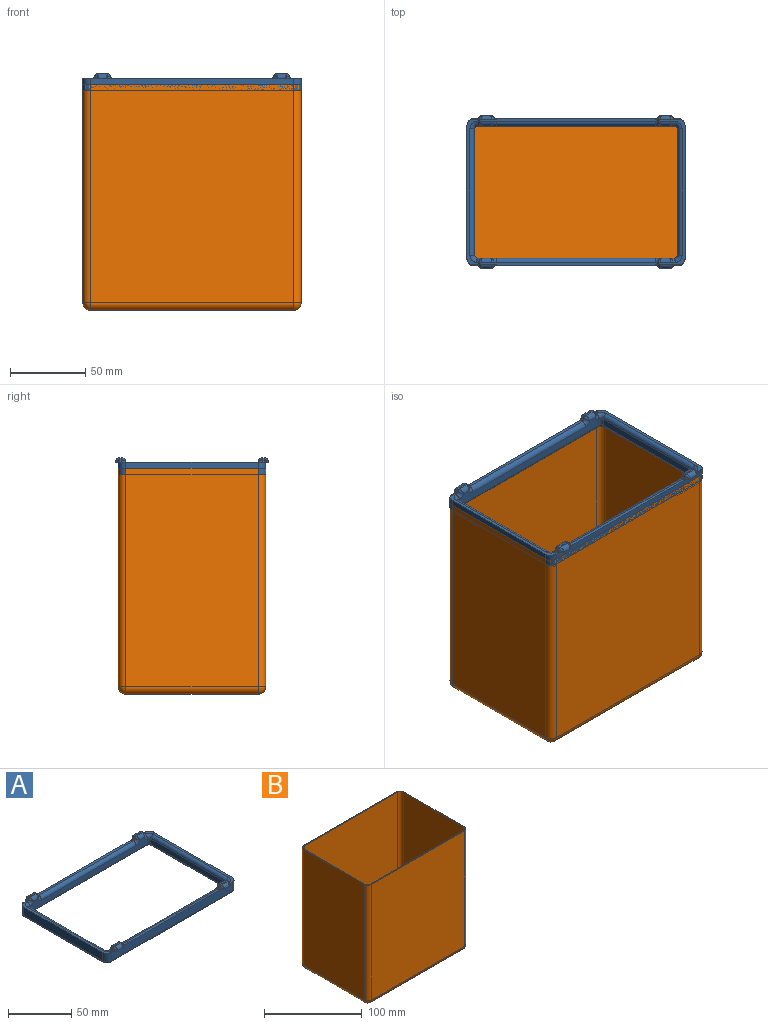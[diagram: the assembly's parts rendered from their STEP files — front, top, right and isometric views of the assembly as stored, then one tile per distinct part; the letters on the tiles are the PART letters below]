
ASSEMBLY  parts=2 mates=1
PART A: 129 faces, bbox 146.3x101.7x13.1 mm
  f0: plane 95.82x6.5mm, normal (0,0,1), area 207mm2, adj f4,f13,f16,f68,f70,f86,f88,f90
  f1: plane 105.79x2.02mm, normal (0,0,1), area 210.9mm2, adj f11,f60,f66,f73,f111,f123
  f2: plane 105.79x2.02mm, normal (0,0,1), area 210.9mm2, adj f5,f64,f72,f104,f105,f117
  f3: plane 95.82x6.5mm, normal (0,0,1), area 207mm2, adj f6,f14,f15,f58,f62,f87,f89,f91
  f4: plane 87.62x8mm, normal (1,0,0), area 701mm2, adj f0,f13,f16,f23
  f5: plane 134.77x8.83mm, normal (0,1,0), area 1078.4mm2, adj f2,f13,f14,f22,f37,f38,f39,f42
  f6: plane 87.62x8mm, normal (-1,0,0), area 701mm2, adj f3,f14,f15,f18
  f7: plane 130.77x8mm, normal (0,-1,0), area 694.7mm2, adj f30,f34,f36,f94,f95,f98,f99,f102
  f8: plane 83.62x5mm, normal (-1,0,0), area 418.1mm2, adj f27,f33,f36,f88
  f9: plane 130.77x8mm, normal (0,1,0), area 694.7mm2, adj f25,f27,f28,f73,f74,f75,f78,f79
  f10: plane 83.62x5mm, normal (1,0,0), area 418.1mm2, adj f25,f29,f30,f89
  f11: plane 134.77x8.83mm, normal (0,-1,0), area 1078.4mm2, adj f1,f15,f16,f19,f47,f48,f51,f53
  f12: plane 140.77x93.62mm, normal (0,0,-1), area 470.8mm2, adj f17,f18,f19,f20,f21,f22,f23,f24
  f13: cylinder r=5mm len=8mm, axis (0,0,-1), area 62.6mm2, adj f0,f4,f5,f24,f110
  f14: cylinder r=5mm len=8mm, axis (0,0,1), area 62.6mm2, adj f3,f5,f6,f20,f122
  f15: cylinder r=5mm len=8mm, axis (0,0,-1), area 62.6mm2, adj f3,f6,f11,f17,f128
  f16: cylinder r=5mm len=8mm, axis (0,0,1), area 62.6mm2, adj f0,f4,f11,f21,f116
  f17: torus R=3mm, axis (0,0,1), area 21.1mm2, adj f12,f15,f18,f19
  f18: cylinder r=2mm len=87.62mm, axis (0,-1,0), area 275.3mm2, adj f6,f12,f17,f20
  f19: cylinder r=2mm len=134.77mm, axis (1,0,0), area 423.4mm2, adj f11,f12,f17,f21
  f20: torus R=3mm, axis (0,0,1), area 21.1mm2, adj f12,f14,f18,f22
  f21: torus R=3mm, axis (0,0,1), area 21.1mm2, adj f12,f16,f19,f23
  f22: cylinder r=2mm len=134.77mm, axis (-1,0,0), area 423.4mm2, adj f5,f12,f20,f24
  f23: cylinder r=2mm len=87.62mm, axis (0,1,0), area 275.3mm2, adj f4,f12,f21,f24
  f24: torus R=3mm, axis (0,0,1), area 21.1mm2, adj f12,f13,f22,f23
  f25: cylinder r=2mm len=5.03mm, axis (0,0,1), area 15.7mm2, adj f9,f10,f26,f85,f87
  f26: torus R=4mm, axis (0,0,1), area 13.5mm2, adj f12,f25,f28,f29
  f27: cylinder r=2mm len=5.03mm, axis (0,0,-1), area 15.7mm2, adj f8,f9,f31,f84,f86
  f28: cylinder r=2mm len=130.77mm, axis (-1,0,0), area 410.8mm2, adj f9,f12,f26,f31
  f29: cylinder r=2mm len=83.62mm, axis (0,1,0), area 262.7mm2, adj f10,f12,f26,f32
  f30: cylinder r=2mm len=5.03mm, axis (0,0,-1), area 15.7mm2, adj f7,f10,f32,f91,f93
  f31: torus R=4mm, axis (0,0,1), area 13.5mm2, adj f12,f27,f28,f33
  f32: torus R=4mm, axis (0,0,1), area 13.5mm2, adj f12,f29,f30,f34
  f33: cylinder r=2mm len=83.62mm, axis (0,-1,0), area 262.7mm2, adj f8,f12,f31,f35
  f34: cylinder r=2mm len=130.77mm, axis (1,0,0), area 410.8mm2, adj f7,f12,f32,f35
  f35: torus R=4mm, axis (0,0,1), area 13.5mm2, adj f12,f33,f34,f36
  f36: cylinder r=2mm len=5.03mm, axis (0,0,1), area 15.7mm2, adj f7,f8,f35,f90,f92
  f37: plane 10x2mm, normal (0,0,-1), area 18.1mm2, adj f5,f38,f39,f40,f117,f121
  f38: plane 0.95x0.89mm, normal (-1,0,0), area 0.4mm2, adj f5,f37,f121
  f39: plane 0.96x0.89mm, normal (1,0,0), area 0.4mm2, adj f5,f37,f117
  f40: plane 4.73x0.1mm, normal (0,1,0), area 0.5mm2, adj f37,f117,f119,f121
  f41: plane 7x1.1mm, normal (0,0,1), area 7.7mm2, adj f61,f63,f99,f119
  f42: plane 10x2mm, normal (0,0,-1), area 18.1mm2, adj f5,f43,f44,f45,f105,f109
  f43: plane 0.96x0.89mm, normal (-1,0,0), area 0.4mm2, adj f5,f42,f105
  f44: plane 0.95x0.89mm, normal (1,0,0), area 0.4mm2, adj f5,f42,f109
  f45: plane 4.73x0.1mm, normal (0,1,0), area 0.5mm2, adj f42,f105,f107,f109
  f46: plane 7x1.1mm, normal (0,0,1), area 7.7mm2, adj f69,f71,f98,f107
  f47: plane 0.96x0.89mm, normal (1,0,0), area 0.4mm2, adj f11,f51,f123
  f48: plane 0.95x0.89mm, normal (-1,0,0), area 0.4mm2, adj f11,f51,f127
  f49: plane 4.73x0.1mm, normal (0,-1,0), area 0.5mm2, adj f51,f123,f125,f127
  f50: plane 7x1.1mm, normal (0,0,1), area 7.7mm2, adj f57,f59,f79,f125
  f51: plane 10x2mm, normal (0,0,-1), area 18.1mm2, adj f11,f47,f48,f49,f123,f127
  f52: plane 4.73x0.1mm, normal (0,-1,0), area 0.5mm2, adj f56,f111,f113,f115
  f53: plane 0.95x0.89mm, normal (1,0,0), area 0.4mm2, adj f11,f56,f115
  f54: plane 0.96x0.89mm, normal (-1,0,0), area 0.4mm2, adj f11,f56,f111
  f55: plane 7x1.1mm, normal (0,0,1), area 7.7mm2, adj f65,f67,f78,f113
  f56: plane 10x2mm, normal (0,0,-1), area 18.1mm2, adj f11,f52,f53,f54,f111,f115
  f57: cylinder r=1.5mm len=1.5mm, axis (0,1,0), area 2.6mm2, adj f50,f58,f81,f126
  f58: cylinder r=1.5mm len=1.5mm, axis (0,-1,0), area 2.6mm2, adj f3,f57,f83,f85,f127
  f59: cylinder r=1.5mm len=1.5mm, axis (0,-1,0), area 2.6mm2, adj f50,f60,f77,f124
  f60: cylinder r=1.5mm len=1.5mm, axis (0,1,0), area 2.6mm2, adj f1,f59,f75,f123
  f61: cylinder r=1.5mm len=1.5mm, axis (0,1,0), area 2.6mm2, adj f41,f62,f97,f120
  f62: cylinder r=1.5mm len=1.5mm, axis (0,-1,0), area 2.6mm2, adj f3,f61,f93,f95,f121
  f63: cylinder r=1.5mm len=1.5mm, axis (0,-1,0), area 2.6mm2, adj f41,f64,f101,f118
  f64: cylinder r=1.5mm len=1.5mm, axis (0,1,0), area 2.6mm2, adj f2,f63,f103,f117
  f65: cylinder r=1.5mm len=1.5mm, axis (0,1,0), area 2.6mm2, adj f55,f66,f76,f112
  f66: cylinder r=1.5mm len=1.5mm, axis (0,-1,0), area 2.6mm2, adj f1,f65,f74,f111
  f67: cylinder r=1.5mm len=1.5mm, axis (0,-1,0), area 2.6mm2, adj f55,f68,f80,f114
  f68: cylinder r=1.5mm len=1.5mm, axis (0,1,0), area 2.6mm2, adj f0,f67,f82,f84,f115
  f69: cylinder r=1.5mm len=1.5mm, axis (0,-1,0), area 2.6mm2, adj f46,f70,f96,f108
  f70: cylinder r=1.5mm len=1.5mm, axis (0,1,0), area 2.6mm2, adj f0,f69,f92,f94,f109
  f71: cylinder r=1.5mm len=1.5mm, axis (0,1,0), area 2.6mm2, adj f46,f72,f100,f106
  f72: cylinder r=1.5mm len=1.5mm, axis (0,-1,0), area 2.6mm2, adj f2,f71,f102,f105
  f73: cylinder r=3mm len=105.77mm, axis (1,0,0), area 498.4mm2, adj f1,f9,f74,f75
  f74: torus R=4.5mm, axis (0,-1,0), area 16.7mm2, adj f9,f66,f73,f76
  f75: torus R=4.5mm, axis (0,-1,0), area 16.7mm2, adj f9,f60,f73,f77
  f76: bspline ~3.79x3mm, area 6.2mm2, adj f65,f74,f78
  f77: bspline ~3.79x3mm, area 6.1mm2, adj f59,f75,f79
  f78: cylinder r=3mm len=7mm, axis (1,0,0), area 27.1mm2, adj f9,f55,f76,f80
  f79: cylinder r=3mm len=7mm, axis (1,0,0), area 27.1mm2, adj f9,f50,f77,f81
  f80: bspline ~3.79x3mm, area 6.1mm2, adj f67,f78,f82
  f81: bspline ~3.79x3mm, area 6.2mm2, adj f57,f79,f83
  f82: torus R=4.5mm, axis (0,-1,0), area 15.3mm2, adj f9,f68,f80,f84
  f83: torus R=4.5mm, axis (0,-1,0), area 15.3mm2, adj f9,f58,f81,f85
  f84: bspline ~3.07x3.06mm, area 0.5mm2, adj f27,f68,f82,f86
  f85: bspline ~3.07x3.06mm, area 0.5mm2, adj f25,f58,f83,f87
  f86: torus R=5mm, axis (0,0,1), area 21.4mm2, adj f0,f27,f84,f88
  f87: torus R=5mm, axis (0,0,1), area 21.4mm2, adj f3,f25,f85,f89
  f88: cylinder r=3mm len=83.62mm, axis (0,1,0), area 394mm2, adj f0,f8,f86,f90
  f89: cylinder r=3mm len=83.62mm, axis (0,-1,0), area 394mm2, adj f3,f10,f87,f91
  f90: torus R=5mm, axis (0,0,1), area 21.4mm2, adj f0,f36,f88,f92
  f91: torus R=5mm, axis (0,0,1), area 21.4mm2, adj f3,f30,f89,f93
  f92: bspline ~3.07x3.06mm, area 0.5mm2, adj f36,f70,f90,f94
  f93: bspline ~3.07x3.06mm, area 0.5mm2, adj f30,f62,f91,f95
  f94: torus R=4.5mm, axis (0,-1,0), area 15.3mm2, adj f7,f70,f92,f96
  f95: torus R=4.5mm, axis (0,-1,0), area 15.3mm2, adj f7,f62,f93,f97
  f96: bspline ~3.79x3mm, area 6.2mm2, adj f69,f94,f98
  f97: bspline ~3.79x3mm, area 6.1mm2, adj f61,f95,f99
  f98: cylinder r=3mm len=7mm, axis (-1,0,0), area 27.1mm2, adj f7,f46,f96,f100
  f99: cylinder r=3mm len=7mm, axis (-1,0,0), area 27.1mm2, adj f7,f41,f97,f101
  f100: bspline ~3.79x3mm, area 6.1mm2, adj f71,f98,f102
  f101: bspline ~3.79x3mm, area 6.2mm2, adj f63,f99,f103
  f102: torus R=4.5mm, axis (0,-1,0), area 16.7mm2, adj f7,f72,f100,f104
  f103: torus R=4.5mm, axis (0,-1,0), area 16.7mm2, adj f7,f64,f101,f104
  f104: cylinder r=3mm len=105.77mm, axis (-1,0,0), area 498.4mm2, adj f2,f7,f102,f103
  f105: torus R=4.4mm, axis (0,-1,0), area 5.8mm2, adj f2,f5,f42,f43,f45,f72,f106
  f106: bspline ~3.1x2.9mm, area 4.7mm2, adj f71,f105,f107
  f107: cylinder r=2.9mm len=7mm, axis (1,0,0), area 26.6mm2, adj f45,f46,f106,f108
  f108: bspline ~2.9x2.9mm, area 6.7mm2, adj f69,f107,f109
  f109: torus R=4.4mm, axis (0,-1,0), area 5.5mm2, adj f5,f42,f44,f45,f70,f108,f110
  f110: cylinder r=2.9mm len=4.36mm, axis (-1,0,0), area 2.7mm2, adj f0,f5,f13,f109
  f111: torus R=4.4mm, axis (0,-1,0), area 5.8mm2, adj f1,f11,f52,f54,f56,f66,f112
  f112: bspline ~3.38x2.9mm, area 6.7mm2, adj f65,f111,f113
  f113: cylinder r=2.9mm len=7mm, axis (-1,0,0), area 26.6mm2, adj f52,f55,f112,f114
  f114: bspline ~3.1x2.9mm, area 4.7mm2, adj f67,f113,f115
  f115: torus R=4.4mm, axis (0,-1,0), area 5.5mm2, adj f11,f52,f53,f56,f68,f114,f116
  f116: cylinder r=2.9mm len=4.36mm, axis (1,0,0), area 2.7mm2, adj f0,f11,f16,f115
  f117: torus R=4.4mm, axis (0,1,0), area 5.8mm2, adj f2,f5,f37,f39,f40,f64,f118
  f118: bspline ~3.38x2.9mm, area 6.7mm2, adj f63,f117,f119
  f119: cylinder r=2.9mm len=7mm, axis (1,0,0), area 26.6mm2, adj f40,f41,f118,f120
  f120: bspline ~3.1x2.9mm, area 4.7mm2, adj f61,f119,f121
  f121: torus R=4.4mm, axis (0,1,0), area 5.5mm2, adj f5,f37,f38,f40,f62,f120,f122
  f122: cylinder r=2.9mm len=4.36mm, axis (-1,0,0), area 2.7mm2, adj f3,f5,f14,f121
  f123: torus R=4.4mm, axis (0,1,0), area 5.8mm2, adj f1,f11,f47,f49,f51,f60,f124
  f124: bspline ~3.1x2.9mm, area 4.7mm2, adj f59,f123,f125
  f125: cylinder r=2.9mm len=7mm, axis (-1,0,0), area 26.6mm2, adj f49,f50,f124,f126
  f126: bspline ~2.9x2.9mm, area 6.7mm2, adj f57,f125,f127
  f127: torus R=4.4mm, axis (0,1,0), area 5.5mm2, adj f11,f48,f49,f51,f58,f126,f128
  f128: cylinder r=2.9mm len=4.36mm, axis (1,0,0), area 2.7mm2, adj f3,f11,f15,f127
PART B: 35 faces, bbox 144.8x97.6x150 mm
  f0: plane 144.77x97.62mm, normal (0,0,1), area 473.1mm2, adj f1,f2,f3,f4,f6,f8,f11,f17
  f1: plane 145x134.77mm, normal (0,1,0), area 19541.6mm2, adj f0,f11,f15,f17
  f2: plane 145x87.62mm, normal (-1,0,0), area 12704.9mm2, adj f0,f8,f14,f17
  f3: plane 145x134.77mm, normal (0,-1,0), area 19541.6mm2, adj f0,f6,f8,f9
  f4: plane 145x87.62mm, normal (1,0,0), area 12704.9mm2, adj f0,f6,f10,f11
  f5: plane 134.77x87.62mm, normal (0,0,-1), area 11808.5mm2, adj f9,f10,f14,f15
  f6: cylinder r=5mm len=145mm, axis (0,0,-1), area 1138.8mm2, adj f0,f3,f4,f7
  f7: sphere r=5mm, area 39.3mm2, adj f6,f9,f10
  f8: cylinder r=5mm len=145mm, axis (0,0,1), area 1138.8mm2, adj f0,f2,f3,f12
  f9: cylinder r=5mm len=134.77mm, axis (1,0,0), area 1058.5mm2, adj f3,f5,f7,f12
  f10: cylinder r=5mm len=87.62mm, axis (0,1,0), area 688.2mm2, adj f4,f5,f7,f13
  f11: cylinder r=5mm len=145mm, axis (0,0,1), area 1138.8mm2, adj f0,f1,f4,f13
  f12: sphere r=5mm, area 39.3mm2, adj f8,f9,f14
  f13: sphere r=5mm, area 39.3mm2, adj f10,f11,f15
  f14: cylinder r=5mm len=87.62mm, axis (0,-1,0), area 688.2mm2, adj f2,f5,f12,f16
  f15: cylinder r=5mm len=134.77mm, axis (-1,0,0), area 1058.5mm2, adj f1,f5,f13,f16
  f16: sphere r=5mm, area 39.3mm2, adj f14,f15,f17
  f17: cylinder r=5mm len=145mm, axis (0,0,-1), area 1138.8mm2, adj f0,f1,f2,f16
  f18: plane 145x134.77mm, normal (0,-1,0), area 19541.6mm2, adj f0,f28,f32,f34
  f19: plane 145x87.62mm, normal (1,0,0), area 12704.9mm2, adj f0,f25,f31,f34
  f20: plane 145x134.77mm, normal (0,1,0), area 19541.6mm2, adj f0,f23,f25,f26
  f21: plane 145x87.62mm, normal (-1,0,0), area 12704.9mm2, adj f0,f23,f27,f28
  f22: plane 134.77x87.62mm, normal (0,0,1), area 11808.5mm2, adj f26,f27,f31,f32
  f23: cylinder r=4mm len=145mm, axis (0,0,-1), area 911.1mm2, adj f0,f20,f21,f24
  f24: sphere r=4mm, area 25.1mm2, adj f23,f26,f27
  f25: cylinder r=4mm len=145mm, axis (0,0,1), area 911.1mm2, adj f0,f19,f20,f29
  f26: cylinder r=4mm len=134.77mm, axis (1,0,0), area 846.8mm2, adj f20,f22,f24,f29
  f27: cylinder r=4mm len=87.62mm, axis (0,1,0), area 550.5mm2, adj f21,f22,f24,f30
  f28: cylinder r=4mm len=145mm, axis (0,0,1), area 911.1mm2, adj f0,f18,f21,f30
  f29: sphere r=4mm, area 25.1mm2, adj f25,f26,f31
  f30: sphere r=4mm, area 25.1mm2, adj f27,f28,f32
  f31: cylinder r=4mm len=87.62mm, axis (0,-1,0), area 550.5mm2, adj f19,f22,f29,f33
  f32: cylinder r=4mm len=134.77mm, axis (-1,0,0), area 846.8mm2, adj f18,f22,f30,f33
  f33: sphere r=4mm, area 25.1mm2, adj f31,f32,f34
  f34: cylinder r=4mm len=145mm, axis (0,0,-1), area 911.1mm2, adj f0,f18,f19,f33
PLACE A at identity fixed
PLACE B rot(axis=(0,0,1),180deg) t=(0,0,-144)mm
MATE fastened A.f5 <-> B.f3  axis (0,1,0) through (0,48.81,6)mm
